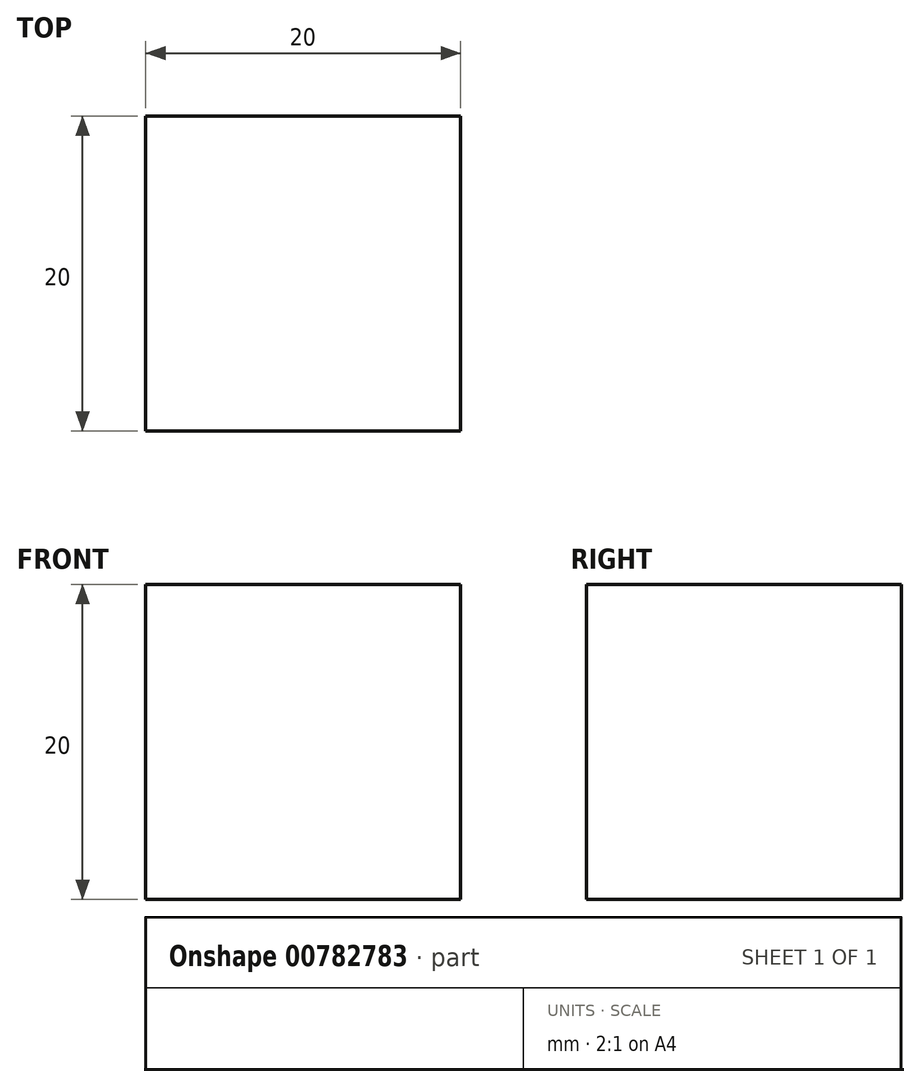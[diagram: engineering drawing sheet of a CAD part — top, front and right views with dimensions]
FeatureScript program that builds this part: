
annotation { "Feature Type Name" : "Feature", "Feature Type Description" : "" }
export const myFeature = defineFeature(function(context is Context, id is Id, definition is map)
    precondition{}
    {
        {
            var Q0;
            Q0=qCreatedBy(makeId("Top.planeOp"),FACE);
            var sketch = newSketch(context, id + "F0", { "sketchPlane" : qUnion([Q0])});
            skLineSegment(sketch, "E0.bottom", {"start": v(-5.1, 3.74) * mm, "end": v(14.9, 3.74) * mm});
            skLineSegment(sketch, "E0.top", {"start": v(-5.1, -16.26) * mm, "end": v(14.9, -16.26) * mm});
            skLineSegment(sketch, "E0.left", {"start": v(-5.1, 3.74) * mm, "end": v(-5.1, -16.26) * mm});
            skLineSegment(sketch, "E0.right", {"start": v(14.9, 3.74) * mm, "end": v(14.9, -16.26) * mm});
            skSolve(sketch);
        }
        {
            var Q0;
            Q0=makeQuery(id+"F0.imprint","IMPRINT",FACE,{"disambiguationData":[TD([[makeQuery(id+"F0.imprint","IMPRINT",EDGE,{"derivedFrom":sQuery(id+"F0.wireOp",EDGE,"E0.bottom")}),-1.0]])]});
            extrude(context, id + "F1", {"entities" : qUnion([Q0]), "depth" : 20 * mm, "offsetDistance" : 25 * mm});
        }
    });
